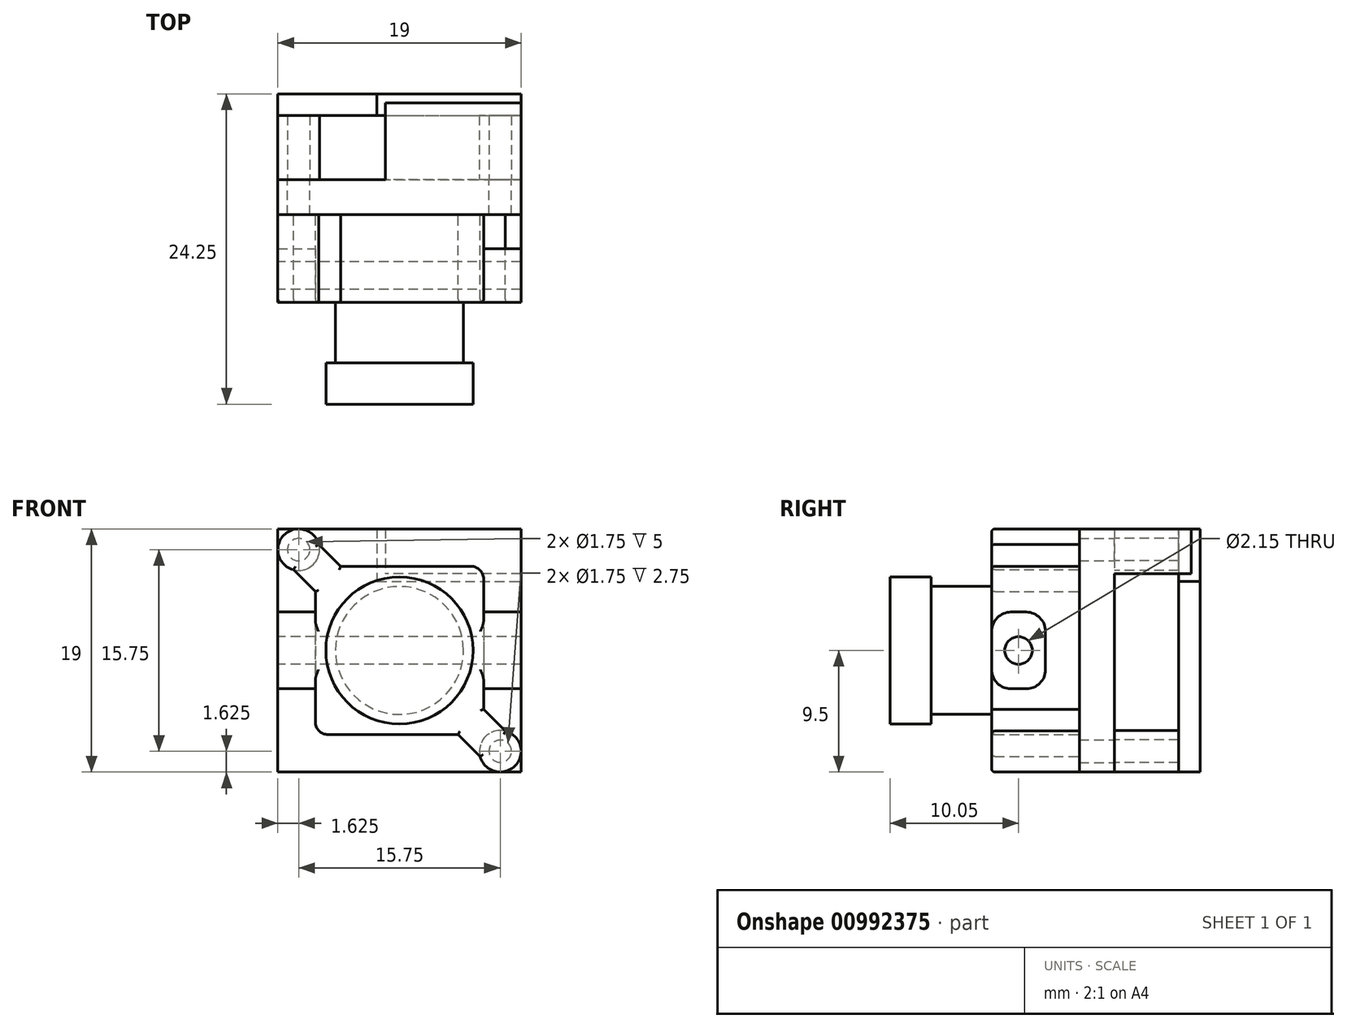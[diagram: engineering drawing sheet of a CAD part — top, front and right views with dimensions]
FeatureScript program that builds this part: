
annotation { "Feature Type Name" : "Feature", "Feature Type Description" : "" }
export const myFeature = defineFeature(function(context is Context, id is Id, definition is map)
    precondition{}
    {
        {
            var Q0;
            Q0=qCreatedBy(makeId("Front.planeOp"),FACE);
            var sketch = newSketch(context, id + "F0", { "sketchPlane" : qUnion([Q0])});
            skLineSegment(sketch, "E0.bottom", {"start": v(-9.5, 9.5) * mm, "end": v(9.5, 9.5) * mm});
            skLineSegment(sketch, "E0.top", {"start": v(-9.5, -9.5) * mm, "end": v(9.5, -9.5) * mm});
            skLineSegment(sketch, "E0.left", {"start": v(-9.5, 9.5) * mm, "end": v(-9.5, -9.5) * mm});
            skLineSegment(sketch, "E0.right", {"start": v(9.5, 9.5) * mm, "end": v(9.5, -9.5) * mm});
            skPoint(sketch, "E1", {"position": v(0, 9.5) * mm});
            skPoint(sketch, "E2", {"position": v(9.5, 0) * mm});
            skCircle(sketch, "E3", {"center": v(-7.88, 7.87) * mm, "radius": 0.88 * mm});
            skCircle(sketch, "E4", {"center": v(7.88, -7.88) * mm, "radius": 0.88 * mm});
            skLineSegment(sketch, "E5", {"start": v(-7.88, 7.87) * mm, "end": v(-7.88, 9.5) * mm, "construction": true});
            skLineSegment(sketch, "E6", {"start": v(-7.88, 7.87) * mm, "end": v(-9.5, 7.87) * mm, "construction": true});
            skLineSegment(sketch, "E7", {"start": v(7.88, -7.88) * mm, "end": v(9.5, -7.88) * mm, "construction": true});
            skLineSegment(sketch, "E8", {"start": v(7.88, -7.88) * mm, "end": v(7.88, -9.5) * mm, "construction": true});
            skSolve(sketch);
        }
        {
            var Q0;
            Q0=makeQuery(id+"F0.imprint","IMPRINT",FACE,{"disambiguationData":[TD([[makeQuery(id+"F0.imprint","IMPRINT",EDGE,{"derivedFrom":sQuery(id+"F0.wireOp",EDGE,"E0.bottom")}),-1.0]])]});
            extrude(context, id + "F1", {"entities" : qUnion([Q0]), "depth" : 2.75 * mm, "offsetDistance" : 25 * mm});
        }
        {
            var Q0;
            Q0=makeQuery(id+"F1.opExtrude","CAP_FACE",FACE,{"disambiguationData":[OSD([sQuery(id+"F0.wireOp",EDGE,"E0.bottom"),sQuery(id+"F0.wireOp",EDGE,"E0.top"),sQuery(id+"F0.wireOp",EDGE,"E0.left"),sQuery(id+"F0.wireOp",EDGE,"E0.right")])],"isStart":true});
            var sketch = newSketch(context, id + "F2", { "sketchPlane" : qUnion([Q0])});
            skLineSegment(sketch, "E9.bottom", {"start": v(-9.5, 9.5) * mm, "end": v(1.1, 9.5) * mm});
            skLineSegment(sketch, "E9.top", {"start": v(-9.5, 6) * mm, "end": v(1.1, 6) * mm});
            skLineSegment(sketch, "E9.left", {"start": v(-9.5, 9.5) * mm, "end": v(-9.5, 6) * mm});
            skLineSegment(sketch, "E9.right", {"start": v(1.1, 9.5) * mm, "end": v(1.1, 6) * mm});
            skSolve(sketch);
        }
        {
            var Q0;
            Q0 = qSketchRegion(id + "F2", true);
            extrude(context, id + "F3", {"entities" : qUnion([Q0]), "operationType" : NewBodyOperationType.ADD, "depth" : 6 * mm, "offsetDistance" : 25 * mm});
        }
        {
            var Q0;
            Q0=makeQuery(id+"F1.opExtrude","CAP_FACE",FACE,{"disambiguationData":[OSD([sQuery(id+"F0.wireOp",EDGE,"E0.bottom"),sQuery(id+"F0.wireOp",EDGE,"E0.top"),sQuery(id+"F0.wireOp",EDGE,"E0.left"),sQuery(id+"F0.wireOp",EDGE,"E0.right")])],"isStart":false});
            var sketch = newSketch(context, id + "F4", { "sketchPlane" : qUnion([Q0])});
            skCircle(sketch, "E10", {"center": v(-7.88, 7.88) * mm, "radius": 1.63 * mm});
            skPoint(sketch, "E11", {"position": v(-7.88, 9.5) * mm});
            skPoint(sketch, "E12", {"position": v(-9.5, 7.88) * mm});
            skLineSegment(sketch, "E13", {"start": v(9.5, 9.5) * mm, "end": v(-9.5, -9.5) * mm, "construction": true});
            skCircle(sketch, "E14.MirrorC", {"center": v(7.88, -7.87) * mm, "radius": 1.63 * mm});
            skLineSegment(sketch, "E15", {"start": v(-6.3, 8.28) * mm, "end": v(-4.6, 6.58) * mm});
            skLineSegment(sketch, "E16", {"start": v(-7.88, 7.88) * mm, "end": v(0, 0) * mm, "construction": true});
            skLineSegment(sketch, "E17.MirrorCS", {"start": v(-8.28, 6.3) * mm, "end": v(-6.58, 4.6) * mm});
            skLineSegment(sketch, "E18", {"start": v(-6.57, 6.57) * mm, "end": v(6.57, 6.57) * mm});
            skPoint(sketch, "E19", {"position": v(0, 6.57) * mm});
            skLineSegment(sketch, "E20", {"start": v(6.57, 6.57) * mm, "end": v(6.57, -6.57) * mm});
            skLineSegment(sketch, "E21", {"start": v(6.57, -6.57) * mm, "end": v(-6.58, -6.58) * mm});
            skLineSegment(sketch, "E22", {"start": v(-6.58, -6.58) * mm, "end": v(-6.58, 6.57) * mm});
            skPoint(sketch, "E23", {"position": v(6.57, 0) * mm});
            skLineSegment(sketch, "E24.MirrorCS", {"start": v(6.3, -8.28) * mm, "end": v(4.6, -6.57) * mm});
            skLineSegment(sketch, "E25.MirrorCS", {"start": v(8.28, -6.3) * mm, "end": v(6.57, -4.6) * mm});
            skSolve(sketch);
        }
        {
            var Q0;
            Q0 = qSketchRegion(id + "F4", true);
            extrude(context, id + "F5", {"entities" : qUnion([Q0]), "operationType" : NewBodyOperationType.ADD, "depth" : 6.85 * mm, "offsetDistance" : 25 * mm});
        }
        {
            var Q0;
            Q0=makeQuery(id+"F5.opExtrude","CAP_FACE",FACE,{"disambiguationData":[OSD([sQuery(id+"F4.wireOp",EDGE,"E10"),sQuery(id+"F4.wireOp",EDGE,"E14.MirrorC"),sQuery(id+"F4.wireOp",EDGE,"E15"),sQuery(id+"F4.wireOp",EDGE,"E17.MirrorCS"),sQuery(id+"F4.wireOp",EDGE,"E18"),sQuery(id+"F4.wireOp",EDGE,"E20"),sQuery(id+"F4.wireOp",EDGE,"E21"),sQuery(id+"F4.wireOp",EDGE,"E22"),sQuery(id+"F4.wireOp",EDGE,"E24.MirrorCS"),sQuery(id+"F4.wireOp",EDGE,"E25.MirrorCS")])],"isStart":false});
            var sketch = newSketch(context, id + "F6", { "sketchPlane" : qUnion([Q0])});
            skCircle(sketch, "E26", {"center": v(0, 0) * mm, "radius": 5 * mm});
            skSolve(sketch);
        }
        {
            var Q0;
            Q0 = qSketchRegion(id + "F6", true);
            extrude(context, id + "F7", {"entities" : qUnion([Q0]), "operationType" : NewBodyOperationType.ADD, "depth" : 4.72 * mm, "offsetDistance" : 25 * mm});
        }
        {
            var Q0;
            Q0=makeQuery(id+"F7.opExtrude","CAP_FACE",FACE,{"disambiguationData":[OSD([sQuery(id+"F6.wireOp",EDGE,"E26")])],"isStart":false});
            var sketch = newSketch(context, id + "F8", { "sketchPlane" : qUnion([Q0])});
            skCircle(sketch, "E27", {"center": v(0, 0) * mm, "radius": 5.75 * mm});
            skSolve(sketch);
        }
        {
            var Q0;
            Q0 = qSketchRegion(id + "F8", true);
            extrude(context, id + "F9", {"entities" : qUnion([Q0]), "operationType" : NewBodyOperationType.ADD, "depth" : 3.23 * mm, "offsetDistance" : 25 * mm});
        }
        {
            var Q0;
            Q0=makeQuery(id+"F5.opExtrude","SWEPT_FACE",FACE,{"disambiguationData":[OSD([sQuery(id+"F4.wireOp",EDGE,"E22")])]});
            var sketch = newSketch(context, id + "F10", { "sketchPlane" : qUnion([Q0])});
            skLineSegment(sketch, "E28.bottom", {"start": v(5.4, 3) * mm, "end": v(9.6, 3) * mm});
            skLineSegment(sketch, "E28.top", {"start": v(5.4, -3) * mm, "end": v(9.6, -3) * mm});
            skLineSegment(sketch, "E28.left", {"start": v(5.4, 3) * mm, "end": v(5.4, -3) * mm});
            skLineSegment(sketch, "E28.right", {"start": v(9.6, 3) * mm, "end": v(9.6, -3) * mm});
            skPoint(sketch, "E29", {"position": v(5.4, 0) * mm});
            skSolve(sketch);
        }
        {
            var Q0;
            Q0=makeQuery(id+"F10.imprint","IMPRINT",FACE,{"disambiguationData":[TD([[makeQuery(id+"F10.imprint","IMPRINT",EDGE,{"derivedFrom":sQuery(id+"F10.wireOp",EDGE,"E28.bottom")}),-1.0]])]});
            var Q1;
            Q1=makeQuery(id+"F1.opExtrude","CAP_VERTEX",VERTEX,{"disambiguationData":[OSD([sQuery(id+"F0.wireOp",EDGE,"E0.bottom"),sQuery(id+"F0.wireOp",EDGE,"E0.left")])],"isStart":false});
            extrude(context, id + "F11", {"entities" : qUnion([Q0]), "endBound" : BoundingType.UP_TO_VERTEX, "depth" : 25 * mm, "endBoundEntityVertex" : qUnion([Q1]), "offsetDistance" : 25 * mm});
        }
        {
            var Q0;
            Q0=makeQuery(id+"F11.opExtrude","SWEPT_EDGE",EDGE,{"disambiguationData":[OSD([sQuery(id+"F4.wireOp",EDGE,"E22"),sQuery(id+"F10.wireOp",EDGE,"E28.bottom"),sQuery(id+"F10.wireOp",EDGE,"E28.right")])]});
            var Q1;
            Q1=makeQuery(id+"F11.opExtrude","SWEPT_EDGE",EDGE,{"disambiguationData":[OSD([sQuery(id+"F10.wireOp",EDGE,"E28.bottom"),sQuery(id+"F10.wireOp",EDGE,"E28.left")])]});
            var Q2;
            Q2=makeQuery(id+"F11.opExtrude","SWEPT_EDGE",EDGE,{"disambiguationData":[OSD([sQuery(id+"F4.wireOp",EDGE,"E22"),sQuery(id+"F10.wireOp",EDGE,"E28.top"),sQuery(id+"F10.wireOp",EDGE,"E28.right")])]});
            var Q3;
            Q3=makeQuery(id+"F11.opExtrude","SWEPT_EDGE",EDGE,{"disambiguationData":[OSD([sQuery(id+"F10.wireOp",EDGE,"E28.top"),sQuery(id+"F10.wireOp",EDGE,"E28.left")])]});
            fillet(context, id + "F12", {"entities" : qUnion([Q0, Q1, Q2, Q3]), "radius" : 1.5 * mm, "tangentPropagation" : true, "allowEdgeOverflow" : false});
        }
        {
            var Q0;
            Q0=makeQuery(id+"F11.opExtrude","SWEPT_BODY",BODY,{"disambiguationData":[OSD([sQuery(id+"F10.wireOp",EDGE,"E28.bottom"),sQuery(id+"F10.wireOp",EDGE,"E28.top"),sQuery(id+"F10.wireOp",EDGE,"E28.left"),sQuery(id+"F10.wireOp",EDGE,"E28.right")])]});
            var Q1;
            Q1=qCreatedBy(makeId("Right.planeOp"),FACE);
            mirror(context, id + "F13", {"operationType" : NewBodyOperationType.ADD, "entities" : qUnion([Q0]), "mirrorPlane" : qUnion([Q1])});
        }
        {
            var Q0;
            Q0=makeQuery(id+"F11.opExtrude","CAP_FACE",FACE,{"disambiguationData":[OSD([sQuery(id+"F10.wireOp",EDGE,"E28.bottom"),sQuery(id+"F10.wireOp",EDGE,"E28.top"),sQuery(id+"F10.wireOp",EDGE,"E28.left"),sQuery(id+"F10.wireOp",EDGE,"E28.right")])],"isStart":false});
            var sketch = newSketch(context, id + "F14", { "sketchPlane" : qUnion([Q0])});
            skCircle(sketch, "E30", {"center": v(7.5, 0) * mm, "radius": 1.07 * mm});
            skPoint(sketch, "E31", {"position": v(7.5, 3) * mm});
            skPoint(sketch, "E32", {"position": v(5.4, 0) * mm});
            skSolve(sketch);
        }
        {
            var Q0;
            Q0=makeQuery(id+"F14.imprint","IMPRINT",FACE,{"disambiguationData":[TD([[makeQuery(id+"F14.imprint","IMPRINT",EDGE,{"derivedFrom":sQuery(id+"F14.wireOp",EDGE,"E30")}),1.0]])]});
            extrude(context, id + "F15", {"entities" : qUnion([Q0]), "operationType" : NewBodyOperationType.REMOVE, "oppositeDirection" : true, "depth" : 25 * mm, "offsetDistance" : 25 * mm});
        }
        {
            var Q0;
            Q0=makeQuery(id+"F5.opExtrude","CAP_EDGE",EDGE,{"disambiguationData":[OSD([sQuery(id+"F4.wireOp",EDGE,"E18")])],"isStart":false});
            var Q1;
            Q1=makeQuery(id+"F5.opExtrude","CAP_EDGE",EDGE,{"disambiguationData":[OSD([sQuery(id+"F4.wireOp",EDGE,"E15")])],"isStart":false});
            var Q2;
            Q2=makeQuery(id+"F5.opExtrude","CAP_EDGE",EDGE,{"disambiguationData":[OSD([sQuery(id+"F4.wireOp",EDGE,"E10")])],"isStart":false});
            var Q3;
            Q3=makeQuery(id+"F5.opExtrude","CAP_EDGE",EDGE,{"disambiguationData":[OSD([sQuery(id+"F4.wireOp",EDGE,"E17.MirrorCS")])],"isStart":false});
            var Q4;
            Q4=makeQuery(id+"F5.opExtrude","CAP_EDGE",EDGE,{"disambiguationData":[OSD([sQuery(id+"F4.wireOp",EDGE,"E21")])],"isStart":false});
            var Q5;
            {var subQ0=sQuery(id+"F4.wireOp",EDGE,"E22");var subQ3=sQuery(id+"F4.wireOp",EDGE,"E21");Q5=makeQuery(id+"F13.boolean.opBoolean","SPLIT",EDGE,{"disambiguationData":[TD([makeQuery(id+"F5.opExtrude","SWEPT_FACE",FACE,{"disambiguationData":[OSD([subQ3])]})])],"derivedFrom":makeQuery(id+"F5.opExtrude","CAP_EDGE",EDGE,{"disambiguationData":[OSD([subQ0])],"isStart":false})});}
            var Q6;
            {var subQ2=sQuery(id+"F4.wireOp",EDGE,"E22");var subQ3=sQuery(id+"F4.wireOp",EDGE,"E17.MirrorCS");Q6=makeQuery(id+"F13.boolean.opBoolean","SPLIT",EDGE,{"disambiguationData":[TD([makeQuery(id+"F5.opExtrude","SWEPT_FACE",FACE,{"disambiguationData":[OSD([subQ3])]})])],"derivedFrom":makeQuery(id+"F5.opExtrude","CAP_EDGE",EDGE,{"disambiguationData":[OSD([subQ2])],"isStart":false})});}
            var Q7;
            {var subQ3=sQuery(id+"F4.wireOp",EDGE,"E20");var subQ4=sQuery(id+"F4.wireOp",EDGE,"E18");Q7=makeQuery(id+"F13.boolean.opBoolean","SPLIT",EDGE,{"disambiguationData":[TD([makeQuery(id+"F5.opExtrude","SWEPT_FACE",FACE,{"disambiguationData":[OSD([subQ4])]})])],"derivedFrom":makeQuery(id+"F5.opExtrude","CAP_EDGE",EDGE,{"disambiguationData":[OSD([subQ3])],"isStart":false})});}
            var Q8;
            {var subQ2=sQuery(id+"F4.wireOp",EDGE,"E25.MirrorCS");var subQ4=sQuery(id+"F4.wireOp",EDGE,"E20");Q8=makeQuery(id+"F13.boolean.opBoolean","SPLIT",EDGE,{"disambiguationData":[TD([makeQuery(id+"F5.opExtrude","SWEPT_FACE",FACE,{"disambiguationData":[OSD([subQ2])]})])],"derivedFrom":makeQuery(id+"F5.opExtrude","CAP_EDGE",EDGE,{"disambiguationData":[OSD([subQ4])],"isStart":false})});}
            var Q9;
            Q9=makeQuery(id+"F5.opExtrude","CAP_EDGE",EDGE,{"disambiguationData":[OSD([sQuery(id+"F4.wireOp",EDGE,"E24.MirrorCS")])],"isStart":false});
            var Q10;
            Q10=makeQuery(id+"F5.opExtrude","CAP_EDGE",EDGE,{"disambiguationData":[OSD([sQuery(id+"F4.wireOp",EDGE,"E14.MirrorC")])],"isStart":false});
            var Q11;
            Q11=makeQuery(id+"F5.opExtrude","CAP_EDGE",EDGE,{"disambiguationData":[OSD([sQuery(id+"F4.wireOp",EDGE,"E25.MirrorCS")])],"isStart":false});
            fillet(context, id + "F16", {"entities" : qUnion([Q0, Q1, Q2, Q3, Q4, Q5, Q6, Q7, Q8, Q9, Q10, Q11]), "radius" : 0.25 * mm, "tangentPropagation" : true, "allowEdgeOverflow" : false});
        }
        {
            var Q0;
            Q0=makeQuery(id+"F5.opExtrude","SWEPT_EDGE",EDGE,{"disambiguationData":[OSD([sQuery(id+"F4.wireOp",EDGE,"E18"),sQuery(id+"F4.wireOp",EDGE,"E20")])]});
            var Q1;
            Q1=makeQuery(id+"F5.opExtrude","SWEPT_EDGE",EDGE,{"disambiguationData":[OSD([sQuery(id+"F4.wireOp",EDGE,"E21"),sQuery(id+"F4.wireOp",EDGE,"E22")])]});
            fillet(context, id + "F17", {"entities" : qUnion([Q0, Q1]), "radius" : 1 * mm, "tangentPropagation" : true, "allowEdgeOverflow" : false});
        }
        {
            var Q0;
            Q0=makeQuery(id+"F1.opExtrude","CAP_FACE",FACE,{"disambiguationData":[OSD([sQuery(id+"F0.wireOp",EDGE,"E0.bottom"),sQuery(id+"F0.wireOp",EDGE,"E0.top"),sQuery(id+"F0.wireOp",EDGE,"E0.left"),sQuery(id+"F0.wireOp",EDGE,"E0.right")])],"isStart":true});
            var sketch = newSketch(context, id + "F18", { "sketchPlane" : qUnion([Q0])});
            skCircle(sketch, "E33", {"center": v(-7.88, -7.87) * mm, "radius": 1.63 * mm});
            skCircle(sketch, "E34", {"center": v(7.88, 7.88) * mm, "radius": 1.63 * mm});
            skCircle(sketch, "E35.0", {"center": v(7.88, 7.87) * mm, "radius": 0.88 * mm});
            skCircle(sketch, "E36.0", {"center": v(-7.88, -7.88) * mm, "radius": 0.88 * mm});
            skSolve(sketch);
        }
        {
            var Q0;
            Q0 = qSketchRegion(id + "F18", true);
            extrude(context, id + "F19", {"entities" : qUnion([Q0]), "depth" : 5 * mm, "offsetDistance" : 25 * mm});
        }
        {
            var Q0;
            Q0=makeQuery(id+"F19.opExtrude","CAP_FACE",FACE,{"disambiguationData":[OSD([sQuery(id+"F18.wireOp",EDGE,"LPsMf1c1-CtTX-sMXP-XX5z-TjtMNIDVBY9M"),sQuery(id+"F18.wireOp",EDGE,"E34")])],"isStart":false});
            var sketch = newSketch(context, id + "F20", { "sketchPlane" : qUnion([Q0])});
            skLineSegment(sketch, "E37.0", {"start": v(9.5, 9.5) * mm, "end": v(9.5, -9.5) * mm});
            skLineSegment(sketch, "E38.0", {"start": v(9.5, -9.5) * mm, "end": v(-9.5, -9.5) * mm});
            skLineSegment(sketch, "E39.0", {"start": v(9.5, 9.5) * mm, "end": v(1.75, 9.5) * mm});
            skLineSegment(sketch, "E40.0", {"start": v(-9.5, 5.4) * mm, "end": v(-9.5, -9.5) * mm});
            skLineSegment(sketch, "E41", {"start": v(1.75, 9.5) * mm, "end": v(1.75, 5.4) * mm});
            skLineSegment(sketch, "E42", {"start": v(1.75, 5.4) * mm, "end": v(-9.5, 5.4) * mm});
            skPoint(sketch, "E43.orphan", {"position": v(-9.5, 9.5) * mm});
            skSolve(sketch);
        }
        {
            var Q0;
            Q0 = qSketchRegion(id + "F20", true);
            extrude(context, id + "F21", {"entities" : qUnion([Q0]), "operationType" : NewBodyOperationType.ADD, "depth" : 1.7 * mm, "offsetDistance" : 25 * mm});
        }
    });
